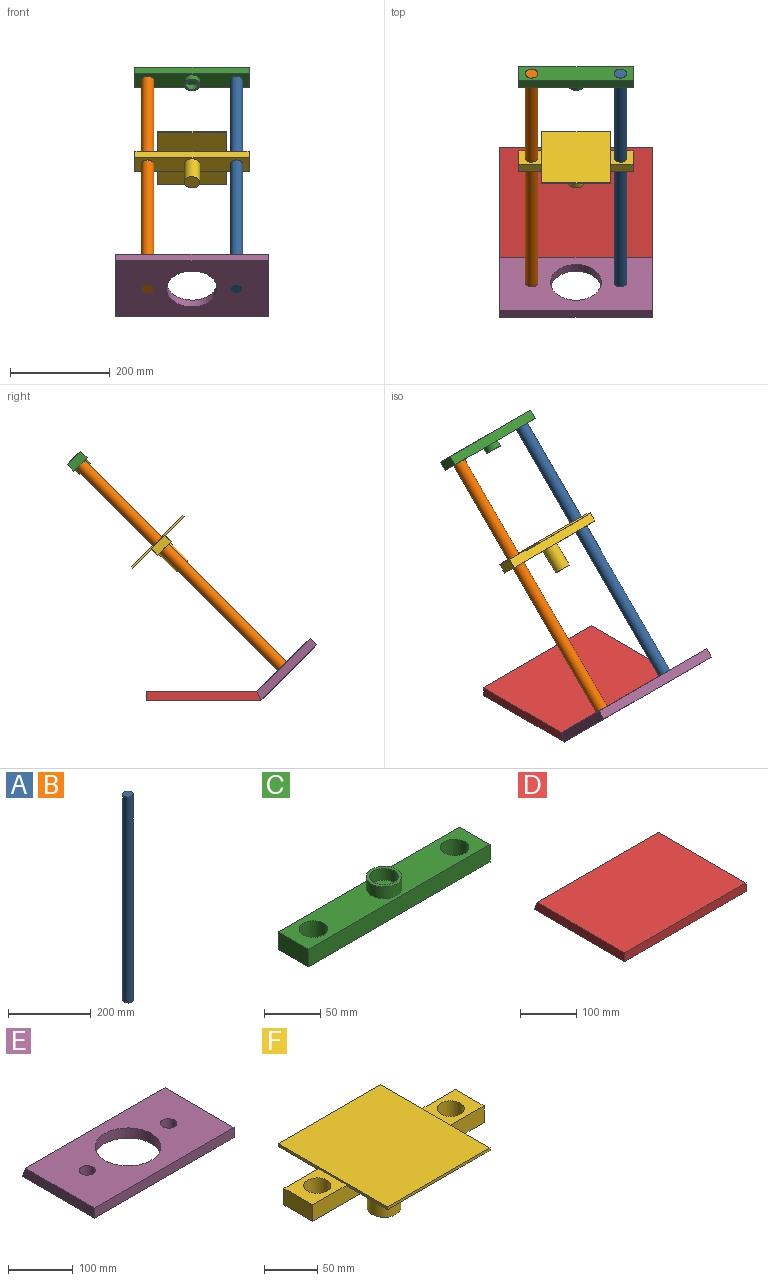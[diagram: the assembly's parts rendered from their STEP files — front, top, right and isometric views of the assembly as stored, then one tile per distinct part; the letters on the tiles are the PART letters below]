
ASSEMBLY  parts=6 mates=6
PART A: 3 faces, bbox 25.4x25.4x609.6 mm
  f0: cylinder r=12.7mm len=609.6mm, axis (0,0,-1), area 48643.9mm2, adj f1,f2
  f1: plane 25.4x25.4mm, normal (0,0,1), area 506.7mm2, adj f0
  f2: plane 25.4x25.4mm, normal (0,0,-1), area 506.7mm2, adj f0
PART B: same geometry as A
PART C: 12 faces, bbox 228.6x38.1x31.8 mm
  f0: plane 38.1x19.05mm, normal (-1,0,0), area 725.8mm2, adj f1,f4,f6,f7
  f1: plane 228.6x19.05mm, normal (0,-1,0), area 4354.8mm2, adj f0,f2,f6,f7
  f2: plane 38.1x19.05mm, normal (1,0,0), area 725.8mm2, adj f1,f4,f6,f7
  f3: cylinder r=12.7mm len=25.4mm, axis (0,0,-1), area 1520.1mm2, adj f6,f7
  f4: plane 228.6x19.05mm, normal (0,1,0), area 4354.8mm2, adj f0,f2,f6,f7
  f5: cylinder r=12.7mm len=25.4mm, axis (0,0,-1), area 1520.1mm2, adj f6,f7
  f6: plane 228.6x38.1mm, normal (0,0,1), area 6904.5mm2, adj f0,f1,f2,f3,f4,f5,f9
  f7: plane 228.6x38.1mm, normal (0,0,-1), area 7696.2mm2, adj f0,f1,f2,f3,f4,f5
  f8: cylinder r=12.7mm len=25.4mm, axis (0,0,-1), area 1013.4mm2, adj f10,f11
  f9: cylinder r=15.88mm len=31.75mm, axis (0,0,-1), area 1266.8mm2, adj f6,f10
  f10: plane 31.75x31.75mm, normal (0,0,1), area 285mm2, adj f8,f9
  f11: plane 25.4x25.4mm, normal (0,0,1), area 506.7mm2, adj f8
PART D: 6 faces, bbox 304.8x228.6x19.1 mm
  f0: plane 228.6x19.05mm, normal (-1,0,0), area 4279.7mm2, adj f1,f3,f4,f5
  f1: plane 304.8x19.05mm, normal (0,-1,0), area 5806.4mm2, adj f0,f2,f3,f4
  f2: plane 228.6x19.05mm, normal (1,0,0), area 4279.7mm2, adj f1,f3,f4,f5
  f3: plane 304.8x220.71mm, normal (0,0,1), area 67272.2mm2, adj f0,f1,f2,f5
  f4: plane 304.8x228.6mm, normal (0,0,-1), area 69677.3mm2, adj f0,f1,f2,f5
  f5: plane 304.8x19.05mm, normal (0,0.92,0.38), area 6284.8mm2, adj f0,f2,f3,f4
PART E: 9 faces, bbox 304.8x158.8x19.1 mm
  f0: plane 158.75x19.05mm, normal (-1,0,0), area 2949mm2, adj f1,f6,f7,f8
  f1: plane 304.8x19.05mm, normal (0,-1,0), area 5806.4mm2, adj f0,f2,f6,f7
  f2: plane 158.75x19.05mm, normal (1,0,0), area 2949mm2, adj f1,f6,f7,f8
  f3: cylinder r=50.8mm len=101.6mm, axis (0,0,-1), area 6080.5mm2, adj f6,f7
  f4: cylinder r=12.7mm len=25.4mm, axis (0,0,-1), area 1520.1mm2, adj f6,f7
  f5: cylinder r=12.7mm len=25.4mm, axis (0,0,-1), area 1520.1mm2, adj f6,f7
  f6: plane 304.8x150.86mm, normal (0,0,1), area 36861.2mm2, adj f0,f1,f2,f3,f4,f5,f8
  f7: plane 304.8x158.75mm, normal (0,0,-1), area 39266.3mm2, adj f0,f1,f2,f3,f4,f5,f8
  f8: plane 304.8x19.05mm, normal (0,0.92,0.38), area 6284.8mm2, adj f0,f2,f6,f7
PART F: 18 faces, bbox 228.6x146.1x71.4 mm
  f0: plane 46.04x38.1mm, normal (0,0,1), area 1247.3mm2, adj f1,f2,f4,f5,f11
  f1: plane 38.1x19.05mm, normal (-1,0,0), area 725.8mm2, adj f0,f2,f5,f8
  f2: plane 228.6x19.05mm, normal (0,-1,0), area 4138.1mm2, adj f0,f1,f3,f7,f8,f9,f10,f11
  f3: plane 38.1x19.05mm, normal (1,0,0), area 725.8mm2, adj f2,f5,f7,f8
  f4: cylinder r=12.7mm len=25.4mm, axis (0,0,-1), area 1520.1mm2, adj f0,f8
  f5: plane 228.6x19.05mm, normal (0,1,0), area 4138.1mm2, adj f0,f1,f3,f7,f8,f10,f11,f15
  f6: cylinder r=12.7mm len=25.4mm, axis (0,0,-1), area 1520.1mm2, adj f7,f8
  f7: plane 46.04x38.1mm, normal (0,0,1), area 1247.3mm2, adj f2,f3,f5,f6,f10
  f8: plane 228.6x38.1mm, normal (0,0,-1), area 6904.5mm2, adj f1,f2,f3,f4,f5,f6,f16
  f9: plane 136.53x53.98mm, normal (0,0,-1), area 7368.9mm2, adj f2,f10,f11,f13
  f10: plane 146.05x3.18mm, normal (1,0,0), area 403.2mm2, adj f2,f5,f7,f9,f12,f13,f14,f15
  f11: plane 146.05x3.18mm, normal (-1,0,0), area 403.2mm2, adj f0,f2,f5,f9,f12,f13,f14,f15
  f12: plane 136.53x3.18mm, normal (0,1,0), area 433.5mm2, adj f10,f11,f14,f15
  f13: plane 136.53x3.18mm, normal (0,-1,0), area 433.5mm2, adj f9,f10,f11,f14
  f14: plane 146.05x136.53mm, normal (0,0,1), area 19939.5mm2, adj f10,f11,f12,f13
  f15: plane 136.53x53.98mm, normal (0,0,-1), area 7368.9mm2, adj f5,f10,f11,f12
  f16: cylinder r=15.88mm len=50.8mm, axis (0,0,1), area 5067.1mm2, adj f8,f17
  f17: plane 31.75x31.75mm, normal (0,0,-1), area 791.7mm2, adj f16
PLACE A rot(axis=(0.68,-0.68,0.28),148.6deg) t=(-86.59,228.57,449.84)mm
PLACE B rot(axis=(-1,0,0),45deg) t=(-264.39,-202.48,18.79)mm
PLACE C rot(axis=(1,0,0),135deg) t=(-175.49,228.57,449.84)mm
PLACE D rot(axis=(0,0,-1),180deg) t=(-175.49,-32.05,-37.34)mm
PLACE E rot(axis=(-1,0,0),45deg) t=(-175.49,-202.48,18.79)mm
PLACE F rot(axis=(-1,0,0),45deg) t=(-175.49,46.91,268.17)mm
MATE fastened B.f0 <-> E.f4  axis (0,-0.71,-0.71) through (-264.39,-202.48,18.79)mm
MATE fastened D.f5 <-> E.f8  axis (0,-0.92,0.38) through (-175.49,-142.41,-27.82)mm
MATE fastened C.f5 <-> A.f0  axis (0,0.71,0.71) through (-86.59,228.57,449.84)mm
MATE slider F.f4 <-> B.f0  axis (0,-0.71,-0.71) through (-264.39,60.38,281.64)mm
MATE fastened A.f0 <-> E.f5  axis (0,-0.71,-0.71) through (-86.59,-202.48,18.79)mm
MATE slider F.f6 <-> A.f0  axis (0,-0.71,-0.71) through (-86.59,46.91,268.17)mm
